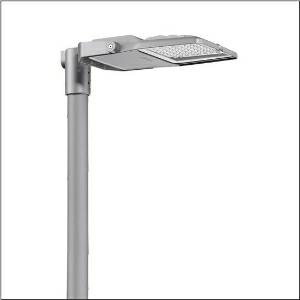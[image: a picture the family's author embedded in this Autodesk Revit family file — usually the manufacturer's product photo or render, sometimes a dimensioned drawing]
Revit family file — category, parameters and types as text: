
# Revit family: floodlight_fl_21_iq_mini___pl43_5xa7771c2a3a_69d2
name_source: partatom
category: Lighting Fixtures
units: mm (PartAtom-declared; Revit-internal decimal feet)

## family parameters
Cut with Voids When Loaded = No
Host = Face
Light Source = No
Part Type = Normal
Room Calculation Point = No
Round Connector Dimension = Use Diameter
Shared = No

## types (1)
- --- (1 x LED, 12520 lm, 87.2 W, 3000K)
    Apparent Load = 87 VA
    CIE Flux Codes = 27 78 99 100 100
    Color Rendering = 70
    Color Temperature = 3000K
    Default Elevation = 1800 mm
    Description = Floodlight FL 21 iQ mini, floodlight, primary light control with lens, of PMMA, primary optical cover: protective disc, of toughened safety glass, transparent, light distribution: PL43, light emission: direct distribution, installation type: surface-mounted, LED, High Power LED, rated luminous flux: 12.520lm, luminous efficacy: 144lm/W, light colour: 730, colour temperature: 3000K, control gear: iQ Comfort/DALI, control: Auto-Match, Temp-Guard, Lumen-Switch, Night-Set, Smart-Wire, Light-Fading, Desk-Remote (wireless, voltage-free reading and setting of iQ features in the workshop via application-optimized NFC function/RFID function), optimised constant luminous flux control (CLO 2.0), with terminal, 6-pole, mains connection: 220..240V, AC, 50/60Hz, start of lifetime: 87W, end of service life: 92W, reduction: 40W, luminaire housing, of diecast aluminium, powder-coated, Siteco® metallic grey (DB 702S), corrosivity category C5 mid according to DIN EN ISO 12944, suitable for swimming pools, chlorine-resistant, sealing non-destructively replaceable, please order mast flange separately, mast bracket, of steel, galvanised, powder-coated, Siteco® metallic grey (DB 702S), protection rating (complete): IP66, insulation class (complete): insulation class II (safety insulation), certification: CE, ENEC, VDE, protection symbol: D, impact resistance: IK08, permissible operating ambient temperature: -40..+40°C, permissible operating ambient temperature for outdoor applications: -40..+50°C, standard: DIN EN 12944, LABS conformity tested according to VDMA 24364:2018-05, packaging unit: 1 piece

Light Distribution: PL43
    Height = 70 mm
    Lamp = 1 x LED
    Lamp Light Flux = 12520 lm
    Lamp Power = 87.2 W
    Lamp count = 1
    Length = 485 mm
    Luminous efficacy = 144 lm/W
    Manufacturer = Siteco
    ModVariant = No
    Model = 5XA7771C2A3A
    Number of Poles = 1
    OnlyDefault = Yes
    Power Factor = 1
    Product Name = Floodlight FL 21 iQ mini | PL43
    Product group = floodlight | pylon annexe
    ProductGroupID = 6201
    Protection Class = Protection class II
    Protection Degree = IP 66
    RLX_Detail_Level = 1
    RLX_Emergency_Light_Flux = 0 lm
    RLX_Emergency_Type = 0
    RLX_Emergency_Type_DB = No
    RlxData = <blob elided: 101357 chars, md5=d60d143c>
    Socket = socket
    Standby Power = 0 W
    System Light Flux = 12520 lm
    System Power = 87 W
    Type Comments = factory setting: luminous flux: 100 % | dim-lin: 254 | 456 mA
    Type Image = l_1007125.jpg
    URL = http://relux.com
    VarID = @adj_183951
    Voltage = 0 V
    Weight = 0.00 kg
    Width = 337 mm

## geometry (parser evidence)
native form markers: Blend x4, Sweep x13
no freeform markers — native parametric forms only
